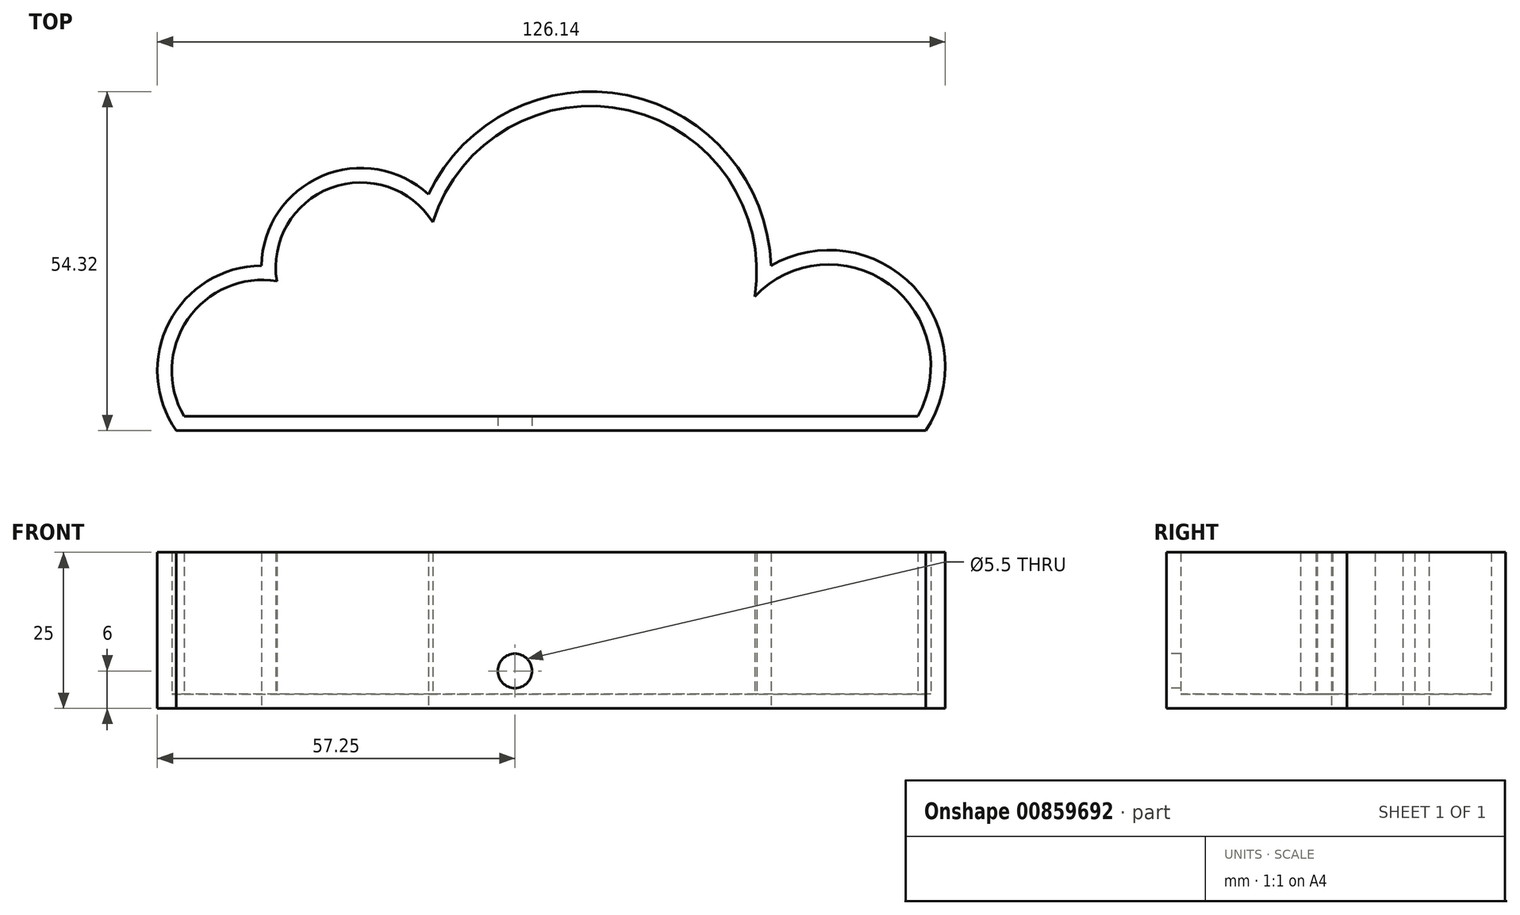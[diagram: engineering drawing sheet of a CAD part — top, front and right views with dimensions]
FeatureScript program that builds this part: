
annotation { "Feature Type Name" : "Feature", "Feature Type Description" : "" }
export const myFeature = defineFeature(function(context is Context, id is Id, definition is map)
    precondition{}
    {
        {
            var Q0;
            Q0=qCreatedBy(makeId("Top.planeOp"),FACE);
            var sketch = newSketch(context, id + "F0", { "sketchPlane" : qUnion([Q0])});
            skLineSegment(sketch, "E0", {"start": v(-54.22, 0) * mm, "end": v(65.78, 0) * mm});
            skArc(sketch, "E1", {"start": v(-40.6, 26.44) * mm, "mid": v(-55.38, 17.33) * mm, "end": v(-54.22, 0) * mm});
            skArc(sketch, "E2", {"start": v(-13.86, 37.84) * mm, "mid": v(-30.91, 40.78) * mm, "end": v(-40.6, 26.44) * mm});
            skArc(sketch, "E3", {"start": v(40.99, 26.44) * mm, "mid": v(18.05, 53.72) * mm, "end": v(-13.86, 37.84) * mm});
            skArc(sketch, "E4", {"start": v(65.78, 0) * mm, "mid": v(63.86, 23.04) * mm, "end": v(40.99, 26.44) * mm});
            skSolve(sketch);
        }
        {
            var Q0;
            Q0 = qSketchRegion(id + "F0", true);
            extrude(context, id + "F1", {"entities" : qUnion([Q0]), "depth" : 25 * mm, "offsetDistance" : 25 * mm});
        }
        {
            var Q0;
            Q0=makeQuery(id+"F1.opExtrude","CAP_FACE",FACE,{"disambiguationData":[OSD([sQuery(id+"F0.wireOp",EDGE,"E0"),sQuery(id+"F0.wireOp",EDGE,"E1"),sQuery(id+"F0.wireOp",EDGE,"E2"),sQuery(id+"F0.wireOp",EDGE,"E3"),sQuery(id+"F0.wireOp",EDGE,"E4")])],"isStart":false});
            shell(context, id + "F2", {"entities" : qUnion([Q0]), "thickness" : 2.3 * mm});
        }
        {
            var Q0;
            Q0=makeQuery(id+"F1.opExtrude","SWEPT_FACE",FACE,{"disambiguationData":[OSD([sQuery(id+"F0.wireOp",EDGE,"E0")])]});
            var sketch = newSketch(context, id + "F3", { "sketchPlane" : qUnion([Q0])});
            skPoint(sketch, "E5", {"position": v(0, 6) * mm});
            skSolve(sketch);
        }
        {
            var Q0;
            Q0=sQuery(id+"F3.wireOp",VERTEX,"E5");
            var Q1;
            Q1=makeQuery(id+"F1.opExtrude","SWEPT_BODY",BODY,{"disambiguationData":[OSD([sQuery(id+"F0.wireOp",EDGE,"E0"),sQuery(id+"F0.wireOp",EDGE,"E1"),sQuery(id+"F0.wireOp",EDGE,"E2"),sQuery(id+"F0.wireOp",EDGE,"E3"),sQuery(id+"F0.wireOp",EDGE,"E4")])]});
            hole(context, id + "F4", {"style" : HoleStyle.SIMPLE, "endStyle" : HoleEndStyle.BLIND, "standardTappedOrClearance" : lookupTablePath({ "fit" : "Normal", "standard" : "ISO", "size" : "M5", "type" : "Clearance" }), "standardBlindInLast" : lookupTablePath({ "fit" : "Standard", "standard" : "ISO", "size" : "M5", "type" : "Clearance" }), "holeDiameter" : 5.5 * mm, "majorDiameter" : 5 * mm, "holeDepth" : 12 * mm, "isTappedThrough" : true, "tappedDepth" : 12 * mm, "tapClearance" : 3, "locations" : qUnion([Q0]), "scope" : qUnion([Q1])});
        }
    });
